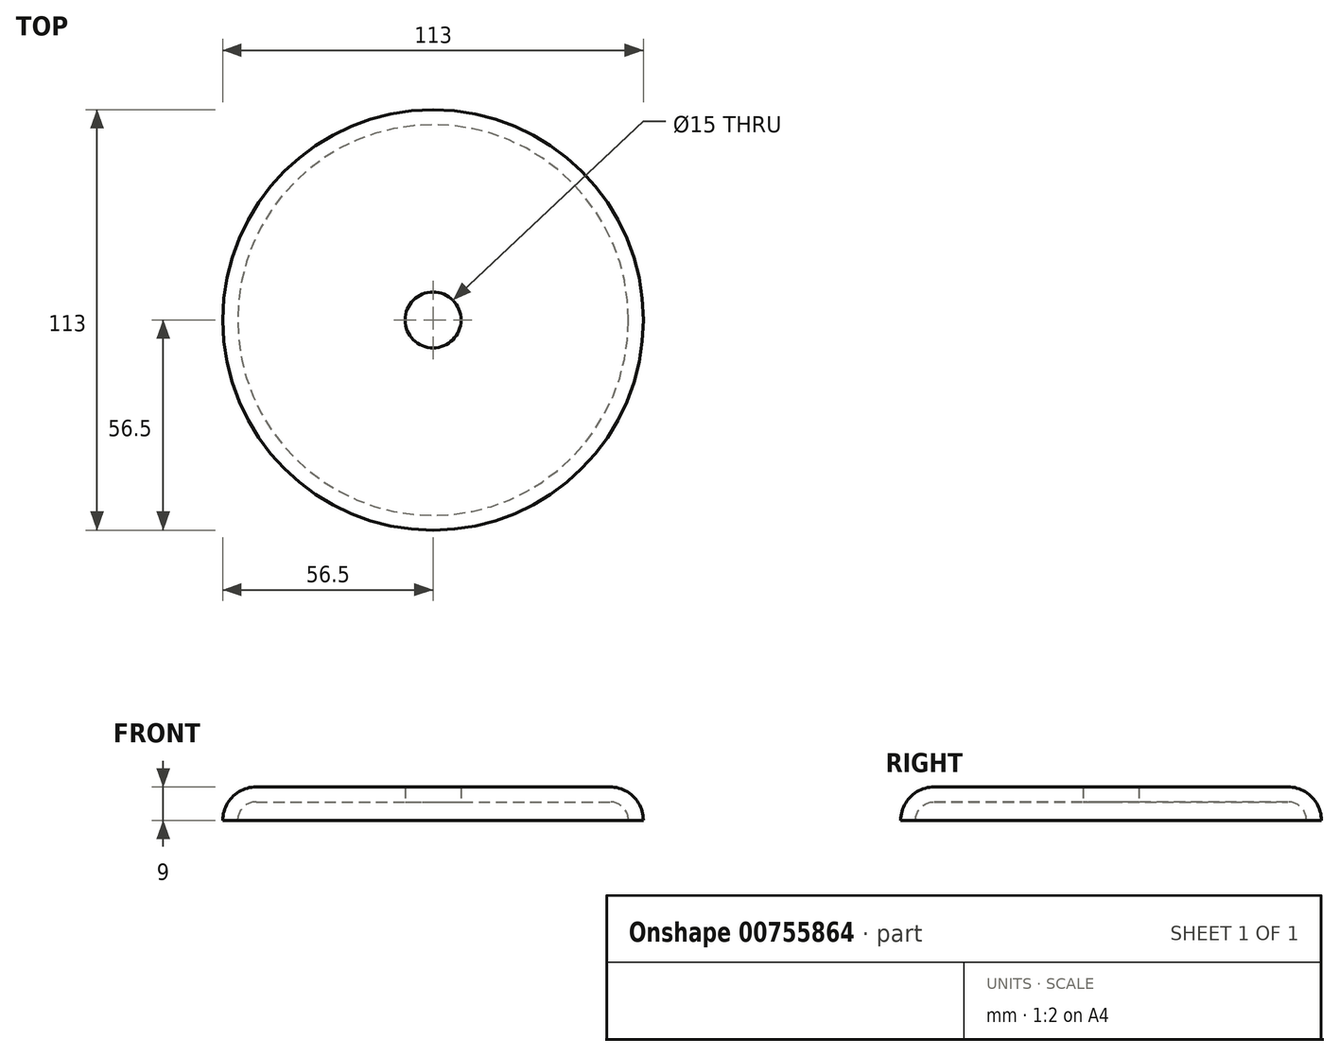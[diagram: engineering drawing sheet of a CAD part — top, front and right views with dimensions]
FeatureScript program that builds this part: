
annotation { "Feature Type Name" : "Feature", "Feature Type Description" : "" }
export const myFeature = defineFeature(function(context is Context, id is Id, definition is map)
    precondition{}
    {
        {
            var Q0;
            Q0=qCreatedBy(makeId("Front.planeOp"),FACE);
            var sketch = newSketch(context, id + "F0", { "sketchPlane" : qUnion([Q0])});
            skLineSegment(sketch, "E0", {"start": v(7.5, 0) * mm, "end": v(47.5, 0) * mm});
            skArc(sketch, "E1", {"start": v(47.5, 0) * mm, "mid": v(53.86, -2.64) * mm, "end": v(56.5, -9) * mm});
            skLineSegment(sketch, "E2", {"start": v(7.5, -4) * mm, "end": v(47.5, -4) * mm});
            skArc(sketch, "E3", {"start": v(47.5, -4) * mm, "mid": v(51.04, -5.46) * mm, "end": v(52.5, -9) * mm});
            skLineSegment(sketch, "E4", {"start": v(52.5, -9) * mm, "end": v(56.5, -9) * mm});
            skLineSegment(sketch, "E5", {"start": v(7.5, 0) * mm, "end": v(7.5, -4) * mm});
            skLineSegment(sketch, "E6", {"start": v(0, 24.6) * mm, "end": v(0, -25.76) * mm, "construction": true});
            skSolve(sketch);
        }
        {
            var Q0;
            Q0=sQuery(id+"F0.wireOp",EDGE,"E5");
            var Q1;
            Q1=sQuery(id+"F0.wireOp",EDGE,"E0");
            var Q2;
            Q2=sQuery(id+"F0.wireOp",EDGE,"E2");
            var Q3;
            Q3=sQuery(id+"F0.wireOp",EDGE,"E1");
            var Q4;
            Q4=sQuery(id+"F0.wireOp",EDGE,"E3");
            var Q5;
            Q5=sQuery(id+"F0.wireOp",EDGE,"E4");
            var Q6;
            Q6=sQuery(id+"F0.wireOp",EDGE,"E6");
            revolve(context, id + "F1", {"bodyType" : ToolBodyType.SURFACE, "surfaceOperationType" : NewSurfaceOperationType.NEW, "surfaceEntities" : qUnion([Q0, Q1, Q2, Q3, Q4, Q5]), "axis" : qUnion([Q6]), "revolveType" : RevolveType.FULL});
        }
    });
